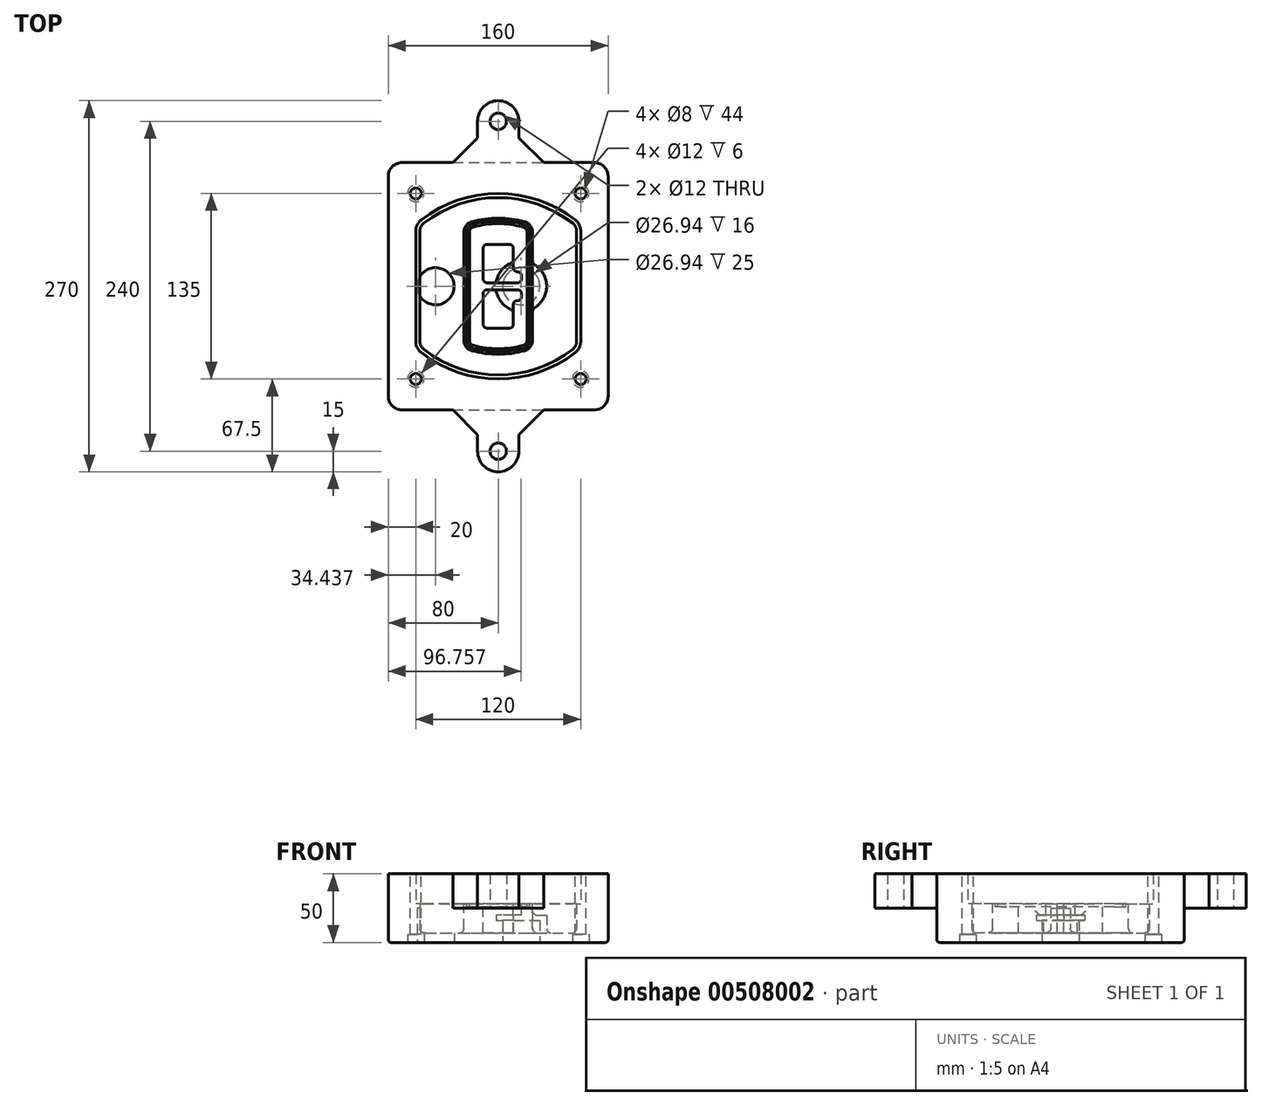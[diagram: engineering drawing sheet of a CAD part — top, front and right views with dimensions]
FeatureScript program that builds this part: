
annotation { "Feature Type Name" : "Feature", "Feature Type Description" : "" }
export const myFeature = defineFeature(function(context is Context, id is Id, definition is map)
    precondition{}
    {
        {
            var Q0;
            Q0=qCreatedBy(makeId("Top.planeOp"),FACE);
            var sketch = newSketch(context, id + "F0", { "sketchPlane" : qUnion([Q0])});
            skPoint(sketch, "E0.rect.middle", {"position": v(0, 0) * mm});
            skLineSegment(sketch, "E1.bottom", {"start": v(-70, -90) * mm, "end": v(70, -90) * mm});
            skLineSegment(sketch, "E1.top", {"start": v(-70, 90) * mm, "end": v(70, 90) * mm});
            skLineSegment(sketch, "E1.left", {"start": v(-80, -80) * mm, "end": v(-80, 80) * mm});
            skLineSegment(sketch, "E1.right", {"start": v(80, -80) * mm, "end": v(80, 80) * mm});
            skLineSegment(sketch, "E2", {"start": v(-80, 90) * mm, "end": v(80, -90) * mm, "construction": true});
            skLineSegment(sketch, "E3", {"start": v(80, 90) * mm, "end": v(-80, -90) * mm, "construction": true});
            skCircle(sketch, "E4", {"center": v(-60, 67.5) * mm, "radius": 4 * mm});
            skCircle(sketch, "E5", {"center": v(60, 67.5) * mm, "radius": 4 * mm});
            skCircle(sketch, "E6", {"center": v(60, -67.5) * mm, "radius": 4 * mm});
            skCircle(sketch, "E7", {"center": v(-60, -67.5) * mm, "radius": 4 * mm});
            skLineSegment(sketch, "E8", {"start": v(-60, 67.5) * mm, "end": v(60, 67.5) * mm, "construction": true});
            skLineSegment(sketch, "E9", {"start": v(60, 67.5) * mm, "end": v(60, -67.5) * mm, "construction": true});
            skLineSegment(sketch, "E10", {"start": v(60, -67.5) * mm, "end": v(-60, -67.5) * mm, "construction": true});
            skLineSegment(sketch, "E11", {"start": v(-60, -67.5) * mm, "end": v(-60, 67.5) * mm, "construction": true});
            skLineSegment(sketch, "E12", {"start": v(-60, 40.3) * mm, "end": v(-60, -40.3) * mm});
            skLineSegment(sketch, "E13", {"start": v(60, 40.3) * mm, "end": v(60, -40.3) * mm});
            skArc(sketch, "E14", {"start": v(56.15, 48.18) * mm, "mid": v(0, 67.5) * mm, "end": v(-56.15, 48.18) * mm});
            skArc(sketch, "E15", {"start": v(-56.15, -48.18) * mm, "mid": v(0, -67.5) * mm, "end": v(56.15, -48.18) * mm});
            skLineSegment(sketch, "E16", {"start": v(-60, 0) * mm, "end": v(60, 0) * mm, "construction": true});
            skPoint(sketch, "E17.visualSharp", {"position": v(-60, -45) * mm});
            skArc(sketch, "E17.filletArc", {"start": v(-60, -40.3) * mm, "mid": v(-58.99, -44.68) * mm, "end": v(-56.15, -48.18) * mm});
            skPoint(sketch, "E18.visualSharp", {"position": v(-60, 45) * mm});
            skArc(sketch, "E18.filletArc", {"start": v(-56.15, 48.18) * mm, "mid": v(-58.99, 44.68) * mm, "end": v(-60, 40.3) * mm});
            skPoint(sketch, "E19.visualSharp", {"position": v(60, 45) * mm});
            skArc(sketch, "E19.filletArc", {"start": v(60, 40.3) * mm, "mid": v(58.99, 44.68) * mm, "end": v(56.15, 48.18) * mm});
            skPoint(sketch, "E20.visualSharp", {"position": v(60, -45) * mm});
            skArc(sketch, "E20.filletArc", {"start": v(56.15, -48.18) * mm, "mid": v(58.99, -44.68) * mm, "end": v(60, -40.3) * mm});
            skPoint(sketch, "E21.visualSharp", {"position": v(-80, 90) * mm});
            skArc(sketch, "E21.filletArc", {"start": v(-70, 90) * mm, "mid": v(-77.07, 87.07) * mm, "end": v(-80, 80) * mm});
            skPoint(sketch, "E22.visualSharp", {"position": v(80, 90) * mm});
            skArc(sketch, "E22.filletArc", {"start": v(80, 80) * mm, "mid": v(77.07, 87.07) * mm, "end": v(70, 90) * mm});
            skPoint(sketch, "E23.visualSharp", {"position": v(80, -90) * mm});
            skArc(sketch, "E23.filletArc", {"start": v(70, -90) * mm, "mid": v(77.07, -87.07) * mm, "end": v(80, -80) * mm});
            skPoint(sketch, "E24.visualSharp", {"position": v(-80, -90) * mm});
            skArc(sketch, "E24.filletArc", {"start": v(-80, -80) * mm, "mid": v(-77.07, -87.07) * mm, "end": v(-70, -90) * mm});
            skArc(sketch, "E25.0", {"start": v(57, 40.3) * mm, "mid": v(56.3, 43.36) * mm, "end": v(54.3, 45.81) * mm});
            skLineSegment(sketch, "E25.1", {"start": v(57, 40.3) * mm, "end": v(57, -40.3) * mm});
            skArc(sketch, "E25.2", {"start": v(54.3, -45.81) * mm, "mid": v(56.3, -43.36) * mm, "end": v(57, -40.3) * mm});
            skArc(sketch, "E25.3", {"start": v(-54.3, -45.81) * mm, "mid": v(0, -64.5) * mm, "end": v(54.3, -45.81) * mm});
            skArc(sketch, "E25.4", {"start": v(-57, -40.3) * mm, "mid": v(-56.3, -43.36) * mm, "end": v(-54.3, -45.81) * mm});
            skArc(sketch, "E25.5", {"start": v(54.3, 45.81) * mm, "mid": v(0, 64.5) * mm, "end": v(-54.3, 45.81) * mm});
            skLineSegment(sketch, "E25.6", {"start": v(-57, 40.3) * mm, "end": v(-57, -40.3) * mm});
            skArc(sketch, "E25.7", {"start": v(-54.3, 45.81) * mm, "mid": v(-56.3, 43.36) * mm, "end": v(-57, 40.3) * mm});
            skArc(sketch, "E26.0", {"start": v(-58.62, 51.33) * mm, "mid": v(-62.58, 46.43) * mm, "end": v(-64, 40.3) * mm});
            skArc(sketch, "E26.1", {"start": v(58.62, 51.33) * mm, "mid": v(0, 71.5) * mm, "end": v(-58.62, 51.33) * mm});
            skArc(sketch, "E26.2", {"start": v(64, 40.3) * mm, "mid": v(62.58, 46.43) * mm, "end": v(58.62, 51.33) * mm});
            skLineSegment(sketch, "E26.3", {"start": v(64, 40.3) * mm, "end": v(64, -40.3) * mm});
            skArc(sketch, "E26.4", {"start": v(58.62, -51.33) * mm, "mid": v(62.58, -46.43) * mm, "end": v(64, -40.3) * mm});
            skLineSegment(sketch, "E26.5", {"start": v(-64, 40.3) * mm, "end": v(-64, -40.3) * mm});
            skArc(sketch, "E26.6", {"start": v(-58.62, -51.33) * mm, "mid": v(0, -71.5) * mm, "end": v(58.62, -51.33) * mm});
            skArc(sketch, "E26.7", {"start": v(-64, -40.3) * mm, "mid": v(-62.58, -46.43) * mm, "end": v(-58.62, -51.33) * mm});
            skSolve(sketch);
        }
        {
            var Q0;
            Q0=makeQuery(id+"F0.imprint","IMPRINT",FACE,{"disambiguationData":[TD([[makeQuery(id+"F0.imprint","IMPRINT",EDGE,{"derivedFrom":sQuery(id+"F0.wireOp",EDGE,"E1.bottom")}),1.0]])]});
            var Q1;
            Q1=makeQuery(id+"F0.imprint","IMPRINT",FACE,{"disambiguationData":[TD([[makeQuery(id+"F0.imprint","IMPRINT",EDGE,{"derivedFrom":sQuery(id+"F0.wireOp",EDGE,"E12")}),1.0]])]});
            var Q2;
            Q2=makeQuery(id+"F0.imprint","IMPRINT",FACE,{"disambiguationData":[TD([[makeQuery(id+"F0.imprint","IMPRINT",EDGE,{"derivedFrom":sQuery(id+"F0.wireOp",EDGE,"E25.0")}),1.0]])]});
            var Q3;
            Q3=makeQuery(id+"F0.imprint","IMPRINT",FACE,{"disambiguationData":[TD([[makeQuery(id+"F0.imprint","IMPRINT",EDGE,{"derivedFrom":sQuery(id+"F0.wireOp",EDGE,"E12")}),-1.0]])]});
            extrude(context, id + "F1", {"entities" : qUnion([Q0, Q1, Q2, Q3]), "oppositeDirection" : true, "depth" : 25 * mm});
        }
        {
            var Q0;
            Q0=makeQuery(id+"F0.imprint","IMPRINT",FACE,{"disambiguationData":[TD([[makeQuery(id+"F0.imprint","IMPRINT",EDGE,{"derivedFrom":sQuery(id+"F0.wireOp",EDGE,"E12")}),1.0]])]});
            extrude(context, id + "F2", {"entities" : qUnion([Q0]), "operationType" : NewBodyOperationType.ADD, "depth" : 3 * mm});
        }
        {
            var Q0;
            Q0=makeQuery(id+"F0.imprint","IMPRINT",FACE,{"disambiguationData":[TD([[makeQuery(id+"F0.imprint","IMPRINT",EDGE,{"derivedFrom":sQuery(id+"F0.wireOp",EDGE,"E25.0")}),1.0]])]});
            extrude(context, id + "F3", {"entities" : qUnion([Q0]), "operationType" : NewBodyOperationType.REMOVE, "oppositeDirection" : true, "depth" : 18 * mm});
        }
        {
            var Q0;
            Q0=makeQuery(id+"F2.opExtrude","CAP_FACE",FACE,{"disambiguationData":[OSD([sQuery(id+"F0.wireOp",EDGE,"E12"),sQuery(id+"F0.wireOp",EDGE,"E13"),sQuery(id+"F0.wireOp",EDGE,"E14"),sQuery(id+"F0.wireOp",EDGE,"E15"),sQuery(id+"F0.wireOp",EDGE,"E17.filletArc"),sQuery(id+"F0.wireOp",EDGE,"E18.filletArc"),sQuery(id+"F0.wireOp",EDGE,"E19.filletArc"),sQuery(id+"F0.wireOp",EDGE,"E20.filletArc"),sQuery(id+"F0.wireOp",EDGE,"E25.0"),sQuery(id+"F0.wireOp",EDGE,"E25.1"),sQuery(id+"F0.wireOp",EDGE,"E25.2"),sQuery(id+"F0.wireOp",EDGE,"E25.3"),sQuery(id+"F0.wireOp",EDGE,"E25.4"),sQuery(id+"F0.wireOp",EDGE,"E25.5"),sQuery(id+"F0.wireOp",EDGE,"E25.6"),sQuery(id+"F0.wireOp",EDGE,"E25.7")])],"isStart":false});
            var sketch = newSketch(context, id + "F4", { "sketchPlane" : qUnion([Q0])});
            skArc(sketch, "E27.0", {"start": v(-19.08, -46.97) * mm, "mid": v(0, -49.5) * mm, "end": v(19.08, -46.97) * mm});
            skArc(sketch, "E28.0", {"start": v(19.08, 46.97) * mm, "mid": v(0, 49.5) * mm, "end": v(-19.08, 46.97) * mm});
            skLineSegment(sketch, "E29", {"start": v(-25, 39.25) * mm, "end": v(-25, -39.25) * mm});
            skLineSegment(sketch, "E30", {"start": v(25, 39.25) * mm, "end": v(25, -39.25) * mm});
            skLineSegment(sketch, "E31", {"start": v(-25, 45.1) * mm, "end": v(25, 45.1) * mm, "construction": true});
            skLineSegment(sketch, "E32", {"start": v(-25, -45.1) * mm, "end": v(25, -45.1) * mm, "construction": true});
            skPoint(sketch, "E33.visualSharp", {"position": v(-25, 45.1) * mm});
            skArc(sketch, "E33.filletArc", {"start": v(-19.08, 46.97) * mm, "mid": v(-23.35, 44.11) * mm, "end": v(-25, 39.25) * mm});
            skPoint(sketch, "E34.visualSharp", {"position": v(25, 45.1) * mm});
            skArc(sketch, "E34.filletArc", {"start": v(25, 39.25) * mm, "mid": v(23.35, 44.11) * mm, "end": v(19.08, 46.97) * mm});
            skPoint(sketch, "E35.visualSharp", {"position": v(25, -45.1) * mm});
            skArc(sketch, "E35.filletArc", {"start": v(19.08, -46.97) * mm, "mid": v(23.35, -44.11) * mm, "end": v(25, -39.25) * mm});
            skPoint(sketch, "E36.visualSharp", {"position": v(-25, -45.1) * mm});
            skArc(sketch, "E36.filletArc", {"start": v(-25, -39.25) * mm, "mid": v(-23.35, -44.11) * mm, "end": v(-19.08, -46.97) * mm});
            skArc(sketch, "E37.0", {"start": v(54.3, 45.81) * mm, "mid": v(0, 64.5) * mm, "end": v(-54.3, 45.81) * mm});
            skArc(sketch, "E37.1", {"start": v(-54.3, 45.81) * mm, "mid": v(-56.3, 43.36) * mm, "end": v(-57, 40.3) * mm});
            skLineSegment(sketch, "E37.2", {"start": v(-57, 40.3) * mm, "end": v(-57, -40.3) * mm});
            skArc(sketch, "E37.3", {"start": v(-57, -40.3) * mm, "mid": v(-56.3, -43.36) * mm, "end": v(-54.3, -45.81) * mm});
            skArc(sketch, "E37.4", {"start": v(-54.3, -45.81) * mm, "mid": v(0, -64.5) * mm, "end": v(54.3, -45.81) * mm});
            skArc(sketch, "E37.5", {"start": v(54.3, -45.81) * mm, "mid": v(56.3, -43.36) * mm, "end": v(57, -40.3) * mm});
            skLineSegment(sketch, "E37.6", {"start": v(57, 40.3) * mm, "end": v(57, -40.3) * mm});
            skArc(sketch, "E37.7", {"start": v(57, 40.3) * mm, "mid": v(56.3, 43.36) * mm, "end": v(54.3, 45.81) * mm});
            skLineSegment(sketch, "E38.0", {"start": v(23, 39.25) * mm, "end": v(23, -39.25) * mm});
            skArc(sketch, "E38.1", {"start": v(18.56, -45.04) * mm, "mid": v(21.76, -42.9) * mm, "end": v(23, -39.25) * mm});
            skArc(sketch, "E38.2", {"start": v(-18.56, -45.04) * mm, "mid": v(0, -47.5) * mm, "end": v(18.56, -45.04) * mm});
            skArc(sketch, "E38.3", {"start": v(-23, -39.25) * mm, "mid": v(-21.76, -42.9) * mm, "end": v(-18.56, -45.04) * mm});
            skLineSegment(sketch, "E38.4", {"start": v(-23, 39.25) * mm, "end": v(-23, -39.25) * mm});
            skArc(sketch, "E38.5", {"start": v(23, 39.25) * mm, "mid": v(21.76, 42.9) * mm, "end": v(18.56, 45.04) * mm});
            skArc(sketch, "E38.6", {"start": v(-18.56, 45.04) * mm, "mid": v(-21.76, 42.9) * mm, "end": v(-23, 39.25) * mm});
            skArc(sketch, "E38.7", {"start": v(18.56, 45.04) * mm, "mid": v(0, 47.5) * mm, "end": v(-18.56, 45.04) * mm});
            skArc(sketch, "E39.0", {"start": v(21, 39.25) * mm, "mid": v(20.18, 41.68) * mm, "end": v(18.04, 43.1) * mm});
            skLineSegment(sketch, "E39.1", {"start": v(21, 39.25) * mm, "end": v(21, -39.25) * mm});
            skArc(sketch, "E39.2", {"start": v(18.04, -43.1) * mm, "mid": v(20.18, -41.68) * mm, "end": v(21, -39.25) * mm});
            skArc(sketch, "E39.3", {"start": v(-18.04, -43.1) * mm, "mid": v(0, -45.5) * mm, "end": v(18.04, -43.1) * mm});
            skArc(sketch, "E39.4", {"start": v(-21, -39.25) * mm, "mid": v(-20.18, -41.68) * mm, "end": v(-18.04, -43.1) * mm});
            skArc(sketch, "E39.5", {"start": v(18.04, 43.1) * mm, "mid": v(0, 45.5) * mm, "end": v(-18.04, 43.1) * mm});
            skLineSegment(sketch, "E39.6", {"start": v(-21, 39.25) * mm, "end": v(-21, -39.25) * mm});
            skArc(sketch, "E39.7", {"start": v(-18.04, 43.1) * mm, "mid": v(-20.18, 41.68) * mm, "end": v(-21, 39.25) * mm});
            skLineSegment(sketch, "E40", {"start": v(-25, 0) * mm, "end": v(25, 0) * mm, "construction": true});
            skLineSegment(sketch, "E41", {"start": v(-11, 5.5) * mm, "end": v(-11, 27.5) * mm});
            skLineSegment(sketch, "E42", {"start": v(-8, 30.5) * mm, "end": v(8, 30.5) * mm});
            skLineSegment(sketch, "E43", {"start": v(11, 27.5) * mm, "end": v(11, 13.5) * mm});
            skLineSegment(sketch, "E44", {"start": v(14, 10.5) * mm, "end": v(14, 10.5) * mm});
            skLineSegment(sketch, "E45", {"start": v(17, 7.5) * mm, "end": v(17, 5.5) * mm});
            skLineSegment(sketch, "E46", {"start": v(14, 2.5) * mm, "end": v(-8, 2.5) * mm});
            skPoint(sketch, "E47.visualSharp", {"position": v(-11, 30.5) * mm});
            skArc(sketch, "E47.filletArc", {"start": v(-8, 30.5) * mm, "mid": v(-10.12, 29.62) * mm, "end": v(-11, 27.5) * mm});
            skPoint(sketch, "E48.visualSharp", {"position": v(11, 30.5) * mm});
            skArc(sketch, "E48.filletArc", {"start": v(11, 27.5) * mm, "mid": v(10.12, 29.62) * mm, "end": v(8, 30.5) * mm});
            skPoint(sketch, "E49.visualSharp", {"position": v(11, 10.5) * mm});
            skArc(sketch, "E49.filletArc", {"start": v(11, 13.5) * mm, "mid": v(11.88, 11.38) * mm, "end": v(14, 10.5) * mm});
            skPoint(sketch, "E50.visualSharp", {"position": v(17, 10.5) * mm});
            skArc(sketch, "E50.filletArc", {"start": v(17, 7.5) * mm, "mid": v(16.12, 9.62) * mm, "end": v(14, 10.5) * mm});
            skPoint(sketch, "E51.visualSharp", {"position": v(17, 2.5) * mm});
            skArc(sketch, "E51.filletArc", {"start": v(14, 2.5) * mm, "mid": v(16.12, 3.38) * mm, "end": v(17, 5.5) * mm});
            skPoint(sketch, "E52.visualSharp", {"position": v(-11, 2.5) * mm});
            skArc(sketch, "E52.filletArc", {"start": v(-11, 5.5) * mm, "mid": v(-10.12, 3.38) * mm, "end": v(-8, 2.5) * mm});
            skLineSegment(sketch, "E53.0.MirrorCS", {"start": v(14, -2.5) * mm, "end": v(-8, -2.5) * mm});
            skArc(sketch, "E54.0.MirrorCS", {"start": v(-11, -5.5) * mm, "mid": v(-10.12, -3.38) * mm, "end": v(-8, -2.5) * mm});
            skLineSegment(sketch, "E55.0.MirrorCS", {"start": v(-11, -5.5) * mm, "end": v(-11, -27.5) * mm});
            skArc(sketch, "E56.0.MirrorCS", {"start": v(-8, -30.5) * mm, "mid": v(-10.12, -29.62) * mm, "end": v(-11, -27.5) * mm});
            skLineSegment(sketch, "E57.0.MirrorCS", {"start": v(-8, -30.5) * mm, "end": v(8, -30.5) * mm});
            skArc(sketch, "E58.0.MirrorCS", {"start": v(11, -27.5) * mm, "mid": v(10.12, -29.62) * mm, "end": v(8, -30.5) * mm});
            skLineSegment(sketch, "E59.0.MirrorCS", {"start": v(11, -27.5) * mm, "end": v(11, -13.5) * mm});
            skArc(sketch, "E60.0.MirrorCS", {"start": v(11, -13.5) * mm, "mid": v(11.88, -11.38) * mm, "end": v(14, -10.5) * mm});
            skArc(sketch, "E61.0.MirrorCS", {"start": v(17, -7.5) * mm, "mid": v(16.12, -9.62) * mm, "end": v(14, -10.5) * mm});
            skLineSegment(sketch, "E62.0.MirrorCS", {"start": v(17, -7.5) * mm, "end": v(17, -5.5) * mm});
            skArc(sketch, "E63.0.MirrorCS", {"start": v(14, -2.5) * mm, "mid": v(16.12, -3.38) * mm, "end": v(17, -5.5) * mm});
            skSolve(sketch);
        }
        {
            var Q0;
            Q0=makeQuery(id+"F4.imprint","IMPRINT",FACE,{"disambiguationData":[TD([[makeQuery(id+"F4.imprint","IMPRINT",EDGE,{"derivedFrom":sQuery(id+"F4.wireOp",EDGE,"E27.0")}),1.0]])]});
            var Q1;
            Q1=makeQuery(id+"F4.imprint","IMPRINT",FACE,{"disambiguationData":[TD([[makeQuery(id+"F4.imprint","IMPRINT",EDGE,{"derivedFrom":sQuery(id+"F4.wireOp",EDGE,"E38.0")}),-1.0]])]});
            var Q2;
            Q2=makeQuery(id+"F4.imprint","IMPRINT",FACE,{"disambiguationData":[TD([[makeQuery(id+"F4.imprint","IMPRINT",EDGE,{"derivedFrom":sQuery(id+"F4.wireOp",EDGE,"E39.0")}),1.0]])]});
            extrude(context, id + "F5", {"entities" : qUnion([Q0, Q1, Q2]), "operationType" : NewBodyOperationType.ADD, "endBound" : BoundingType.UP_TO_NEXT, "oppositeDirection" : true, "depth" : 25 * mm});
        }
        {
            var Q0;
            Q0=makeQuery(id+"F4.imprint","IMPRINT",FACE,{"disambiguationData":[TD([[makeQuery(id+"F4.imprint","IMPRINT",EDGE,{"derivedFrom":sQuery(id+"F4.wireOp",EDGE,"E38.0")}),-1.0]])]});
            extrude(context, id + "F6", {"entities" : qUnion([Q0]), "operationType" : NewBodyOperationType.REMOVE, "oppositeDirection" : true, "depth" : 2 * mm});
        }
        {
            var Q0;
            Q0=makeQuery(id+"F1.opExtrude","CAP_FACE",FACE,{"disambiguationData":[OSD([sQuery(id+"F0.wireOp",EDGE,"E1.bottom"),sQuery(id+"F0.wireOp",EDGE,"E1.top"),sQuery(id+"F0.wireOp",EDGE,"E1.left"),sQuery(id+"F0.wireOp",EDGE,"E1.right"),sQuery(id+"F0.wireOp",EDGE,"E4"),sQuery(id+"F0.wireOp",EDGE,"E5"),sQuery(id+"F0.wireOp",EDGE,"E6"),sQuery(id+"F0.wireOp",EDGE,"E7"),sQuery(id+"F0.wireOp",EDGE,"E21.filletArc"),sQuery(id+"F0.wireOp",EDGE,"E22.filletArc"),sQuery(id+"F0.wireOp",EDGE,"E23.filletArc"),sQuery(id+"F0.wireOp",EDGE,"E24.filletArc")])],"isStart":false});
            var sketch = newSketch(context, id + "F7", { "sketchPlane" : qUnion([Q0])});
            skCircle(sketch, "E64", {"center": v(16.76, 0) * mm, "radius": 13.47 * mm});
            skCircle(sketch, "E65", {"center": v(-45.56, 0) * mm, "radius": 13.47 * mm});
            skLineSegment(sketch, "E66", {"start": v(80, 0) * mm, "end": v(-80, 0) * mm});
            skCircle(sketch, "E67", {"center": v(16.76, 0) * mm, "radius": 18.47 * mm});
            skCircle(sketch, "E68", {"center": v(60, -67.5) * mm, "radius": 6 * mm});
            skCircle(sketch, "E69", {"center": v(-60, -67.5) * mm, "radius": 6 * mm});
            skCircle(sketch, "E70", {"center": v(-60, 67.5) * mm, "radius": 6 * mm});
            skCircle(sketch, "E71", {"center": v(60, 67.5) * mm, "radius": 6 * mm});
            skSolve(sketch);
        }
        {
            var Q0;
            {var subQ1=sQuery(id+"F7.wireOp",EDGE,"E66");var subQ4=sQuery(id+"F7.wireOp",EDGE,"E64");var subQ6=makeQuery(id+"F7.imprint","INTERSECT",VERTEX,{"disambiguationData":[OD(0.0)],"derivedFrom":[subQ4,subQ1]});Q0=makeQuery(id+"F7.imprint","IMPRINT",FACE,{"disambiguationData":[TD([[makeQuery(id+"F7.imprint","IMPRINT",EDGE,{"disambiguationData":[TD([[subQ6,-1.0]])],"derivedFrom":subQ4}),-1.0]])]});}
            var Q1;
            {var subQ0=sQuery(id+"F7.wireOp",EDGE,"E66");var subQ1=sQuery(id+"F7.wireOp",EDGE,"E64");var subQ3=makeQuery(id+"F7.imprint","INTERSECT",VERTEX,{"disambiguationData":[OD(0.0)],"derivedFrom":[subQ1,subQ0]});Q1=makeQuery(id+"F7.imprint","IMPRINT",FACE,{"disambiguationData":[TD([[makeQuery(id+"F7.imprint","IMPRINT",EDGE,{"disambiguationData":[TD([[subQ3,-1.0]])],"derivedFrom":subQ1}),1.0]])]});}
            var Q2;
            {var subQ0=sQuery(id+"F7.wireOp",EDGE,"E66");var subQ1=sQuery(id+"F7.wireOp",EDGE,"E64");var subQ3=makeQuery(id+"F7.imprint","INTERSECT",VERTEX,{"disambiguationData":[OD(0.0)],"derivedFrom":[subQ1,subQ0]});Q2=makeQuery(id+"F7.imprint","IMPRINT",FACE,{"disambiguationData":[TD([[makeQuery(id+"F7.imprint","IMPRINT",EDGE,{"disambiguationData":[TD([[subQ3,1.0]])],"derivedFrom":subQ1}),1.0]])]});}
            var Q3;
            {var subQ1=sQuery(id+"F7.wireOp",EDGE,"E66");var subQ4=sQuery(id+"F7.wireOp",EDGE,"E64");var subQ6=makeQuery(id+"F7.imprint","INTERSECT",VERTEX,{"disambiguationData":[OD(0.0)],"derivedFrom":[subQ4,subQ1]});Q3=makeQuery(id+"F7.imprint","IMPRINT",FACE,{"disambiguationData":[TD([[makeQuery(id+"F7.imprint","IMPRINT",EDGE,{"disambiguationData":[TD([[subQ6,1.0]])],"derivedFrom":subQ4}),-1.0]])]});}
            extrude(context, id + "F8", {"entities" : qUnion([Q0, Q1, Q2, Q3]), "operationType" : NewBodyOperationType.ADD, "oppositeDirection" : true, "depth" : 20 * mm});
        }
        {
            var Q0;
            {var subQ0=sQuery(id+"F7.wireOp",EDGE,"E66");var subQ1=sQuery(id+"F7.wireOp",EDGE,"E64");var subQ3=makeQuery(id+"F7.imprint","INTERSECT",VERTEX,{"disambiguationData":[OD(0.0)],"derivedFrom":[subQ1,subQ0]});Q0=makeQuery(id+"F7.imprint","IMPRINT",FACE,{"disambiguationData":[TD([[makeQuery(id+"F7.imprint","IMPRINT",EDGE,{"disambiguationData":[TD([[subQ3,-1.0]])],"derivedFrom":subQ1}),1.0]])]});}
            var Q1;
            {var subQ0=sQuery(id+"F7.wireOp",EDGE,"E66");var subQ1=sQuery(id+"F7.wireOp",EDGE,"E64");var subQ3=makeQuery(id+"F7.imprint","INTERSECT",VERTEX,{"disambiguationData":[OD(0.0)],"derivedFrom":[subQ1,subQ0]});Q1=makeQuery(id+"F7.imprint","IMPRINT",FACE,{"disambiguationData":[TD([[makeQuery(id+"F7.imprint","IMPRINT",EDGE,{"disambiguationData":[TD([[subQ3,1.0]])],"derivedFrom":subQ1}),1.0]])]});}
            extrude(context, id + "F9", {"entities" : qUnion([Q0, Q1]), "operationType" : NewBodyOperationType.REMOVE, "oppositeDirection" : true, "depth" : 16 * mm});
        }
        {
            var Q0;
            {var subQ0=sQuery(id+"F7.wireOp",EDGE,"E66");var subQ1=sQuery(id+"F7.wireOp",EDGE,"E65");var subQ3=makeQuery(id+"F7.imprint","INTERSECT",VERTEX,{"disambiguationData":[OD(0.0)],"derivedFrom":[subQ1,subQ0]});Q0=makeQuery(id+"F7.imprint","IMPRINT",FACE,{"disambiguationData":[TD([[makeQuery(id+"F7.imprint","IMPRINT",EDGE,{"disambiguationData":[TD([[subQ3,-1.0]])],"derivedFrom":subQ1}),1.0]])]});}
            var Q1;
            {var subQ0=sQuery(id+"F7.wireOp",EDGE,"E66");var subQ1=sQuery(id+"F7.wireOp",EDGE,"E65");var subQ3=makeQuery(id+"F7.imprint","INTERSECT",VERTEX,{"disambiguationData":[OD(0.0)],"derivedFrom":[subQ1,subQ0]});Q1=makeQuery(id+"F7.imprint","IMPRINT",FACE,{"disambiguationData":[TD([[makeQuery(id+"F7.imprint","IMPRINT",EDGE,{"disambiguationData":[TD([[subQ3,1.0]])],"derivedFrom":subQ1}),1.0]])]});}
            extrude(context, id + "F10", {"entities" : qUnion([Q0, Q1]), "operationType" : NewBodyOperationType.REMOVE, "oppositeDirection" : true, "depth" : 25 * mm});
        }
        {
            var Q0;
            Q0=makeQuery(id+"F7.imprint","IMPRINT",FACE,{"disambiguationData":[TD([[makeQuery(id+"F7.imprint","IMPRINT",EDGE,{"derivedFrom":sQuery(id+"F7.wireOp",EDGE,"E68")}),1.0]])]});
            var Q1;
            Q1=makeQuery(id+"F7.imprint","IMPRINT",FACE,{"disambiguationData":[TD([[makeQuery(id+"F7.imprint","IMPRINT",EDGE,{"derivedFrom":makeQuery(id+"F1.opExtrude","CAP_EDGE",EDGE,{"disambiguationData":[OSD([sQuery(id+"F0.wireOp",EDGE,"E5")])],"isStart":false})}),-1.0]])]});
            var Q2;
            Q2=makeQuery(id+"F7.imprint","IMPRINT",FACE,{"disambiguationData":[TD([[makeQuery(id+"F7.imprint","IMPRINT",EDGE,{"derivedFrom":sQuery(id+"F7.wireOp",EDGE,"E69")}),1.0]])]});
            var Q3;
            Q3=makeQuery(id+"F7.imprint","IMPRINT",FACE,{"disambiguationData":[TD([[makeQuery(id+"F7.imprint","IMPRINT",EDGE,{"derivedFrom":makeQuery(id+"F1.opExtrude","CAP_EDGE",EDGE,{"disambiguationData":[OSD([sQuery(id+"F0.wireOp",EDGE,"E4")])],"isStart":false})}),-1.0]])]});
            var Q4;
            Q4=makeQuery(id+"F7.imprint","IMPRINT",FACE,{"disambiguationData":[TD([[makeQuery(id+"F7.imprint","IMPRINT",EDGE,{"derivedFrom":sQuery(id+"F7.wireOp",EDGE,"E70")}),1.0]])]});
            var Q5;
            Q5=makeQuery(id+"F7.imprint","IMPRINT",FACE,{"disambiguationData":[TD([[makeQuery(id+"F7.imprint","IMPRINT",EDGE,{"derivedFrom":makeQuery(id+"F1.opExtrude","CAP_EDGE",EDGE,{"disambiguationData":[OSD([sQuery(id+"F0.wireOp",EDGE,"E7")])],"isStart":false})}),-1.0]])]});
            var Q6;
            Q6=makeQuery(id+"F7.imprint","IMPRINT",FACE,{"disambiguationData":[TD([[makeQuery(id+"F7.imprint","IMPRINT",EDGE,{"derivedFrom":sQuery(id+"F7.wireOp",EDGE,"E71")}),1.0]])]});
            var Q7;
            Q7=makeQuery(id+"F7.imprint","IMPRINT",FACE,{"disambiguationData":[TD([[makeQuery(id+"F7.imprint","IMPRINT",EDGE,{"derivedFrom":makeQuery(id+"F1.opExtrude","CAP_EDGE",EDGE,{"disambiguationData":[OSD([sQuery(id+"F0.wireOp",EDGE,"E6")])],"isStart":false})}),-1.0]])]});
            extrude(context, id + "F11", {"entities" : qUnion([Q0, Q1, Q2, Q3, Q4, Q5, Q6, Q7]), "operationType" : NewBodyOperationType.REMOVE, "oppositeDirection" : true, "depth" : 6 * mm});
        }
        {
            var Q0;
            Q0=makeQuery(id+"F9.boolean.opBoolean","COPY",FACE,{"derivedFrom":makeQuery(id+"F9.opExtrude","CAP_FACE",FACE,{"disambiguationData":[OSD([sQuery(id+"F7.wireOp",EDGE,"E64")])],"isStart":false})});
            var sketch = newSketch(context, id + "F12", { "sketchPlane" : qUnion([Q0])});
            skArc(sketch, "E72.0", {"start": v(11, 17.55) * mm, "mid": v(2.57, 11.82) * mm, "end": v(-1.54, 2.5) * mm});
            skArc(sketch, "E72.1", {"start": v(-1.54, -2.5) * mm, "mid": v(2.57, -11.82) * mm, "end": v(11, -17.55) * mm});
            skLineSegment(sketch, "E73", {"start": v(-1.54, -2.5) * mm, "end": v(14, -2.5) * mm});
            skLineSegment(sketch, "E74.0", {"start": v(14, 2.5) * mm, "end": v(-1.54, 2.5) * mm});
            skArc(sketch, "E74.1", {"start": v(14, 2.5) * mm, "mid": v(16.12, 3.38) * mm, "end": v(17, 5.5) * mm});
            skLineSegment(sketch, "E74.2", {"start": v(17, 7.5) * mm, "end": v(17, 5.5) * mm});
            skArc(sketch, "E74.3", {"start": v(17, 7.5) * mm, "mid": v(16.12, 9.62) * mm, "end": v(14, 10.5) * mm});
            skArc(sketch, "E74.4", {"start": v(11, 13.5) * mm, "mid": v(11.88, 11.38) * mm, "end": v(14, 10.5) * mm});
            skLineSegment(sketch, "E74.5", {"start": v(11, 17.55) * mm, "end": v(11, 13.5) * mm});
            skLineSegment(sketch, "E74.7", {"start": v(14, -2.5) * mm, "end": v(-1.54, -2.5) * mm});
            skArc(sketch, "E74.8", {"start": v(14, -2.5) * mm, "mid": v(16.12, -3.38) * mm, "end": v(17, -5.5) * mm});
            skLineSegment(sketch, "E74.9", {"start": v(17, -7.5) * mm, "end": v(17, -5.5) * mm});
            skArc(sketch, "E74.10", {"start": v(17, -7.5) * mm, "mid": v(16.12, -9.62) * mm, "end": v(14, -10.5) * mm});
            skArc(sketch, "E74.11", {"start": v(11, -13.5) * mm, "mid": v(11.88, -11.38) * mm, "end": v(14, -10.5) * mm});
            skLineSegment(sketch, "E74.12", {"start": v(11, -17.55) * mm, "end": v(11, -13.5) * mm});
            skPoint(sketch, "E75.orphan", {"position": v(11, -27.5) * mm});
            skPoint(sketch, "E76.orphan", {"position": v(-8, -2.5) * mm});
            skPoint(sketch, "E77.orphan", {"position": v(-8, 2.5) * mm});
            skPoint(sketch, "E78.orphan", {"position": v(11, 27.5) * mm});
            skSolve(sketch);
        }
        {
            var Q0;
            {var subQ7=sQuery(id+"F12.wireOp",EDGE,"E72.0");var subQ14=sQuery(id+"F12.wireOp",EDGE,"E72.1");var subQ16=sQuery(id+"F12.wireOp",EDGE,"E74.1");var subQ18=sQuery(id+"F12.wireOp",EDGE,"E74.8");Q0=qUnion([makeQuery(id+"F12.imprint","IMPRINT",FACE,{"disambiguationData":[TD([[makeQuery(id+"F12.imprint","IMPRINT",EDGE,{"derivedFrom":subQ7}),1.0]])]}),makeQuery(id+"F12.imprint","IMPRINT",FACE,{"disambiguationData":[TD([[makeQuery(id+"F12.imprint","IMPRINT",EDGE,{"derivedFrom":subQ14}),1.0]])]}),makeQuery(id+"F12.imprint","IMPRINT",FACE,{"disambiguationData":[TD([[makeQuery(id+"F12.imprint","IMPRINT",EDGE,{"derivedFrom":subQ16}),1.0]])]}),makeQuery(id+"F12.imprint","IMPRINT",FACE,{"disambiguationData":[TD([[makeQuery(id+"F12.imprint","IMPRINT",EDGE,{"derivedFrom":subQ18}),-1.0]])]})]);}
            var Q1;
            Q1=makeQuery(id+"F5.boolean.opBoolean","SPLIT",FACE,{"disambiguationData":[TD([makeQuery(id+"F5.opExtrude","SWEPT_FACE",FACE,{"disambiguationData":[OSD([sQuery(id+"F4.wireOp",EDGE,"E41")])]})])],"derivedFrom":makeQuery(id+"F3.boolean.opBoolean","COPY",FACE,{"derivedFrom":makeQuery(id+"F3.opExtrude","CAP_FACE",FACE,{"disambiguationData":[OSD([sQuery(id+"F0.wireOp",EDGE,"E25.0"),sQuery(id+"F0.wireOp",EDGE,"E25.1"),sQuery(id+"F0.wireOp",EDGE,"E25.2"),sQuery(id+"F0.wireOp",EDGE,"E25.3"),sQuery(id+"F0.wireOp",EDGE,"E25.4"),sQuery(id+"F0.wireOp",EDGE,"E25.5"),sQuery(id+"F0.wireOp",EDGE,"E25.6"),sQuery(id+"F0.wireOp",EDGE,"E25.7")])],"isStart":false})})});
            extrude(context, id + "F13", {"entities" : qUnion([Q0]), "operationType" : NewBodyOperationType.REMOVE, "endBound" : BoundingType.UP_TO_SURFACE, "endBoundEntityFace" : qUnion([Q1]), "depth" : 25 * mm});
        }
        {
            var Q0;
            Q0=makeQuery(id+"F3.boolean.opBoolean","COPY",EDGE,{"derivedFrom":makeQuery(id+"F3.opExtrude","CAP_EDGE",EDGE,{"disambiguationData":[OSD([sQuery(id+"F0.wireOp",EDGE,"E25.6")])],"isStart":false})});
            var Q1;
            Q1=makeQuery(id+"F8.boolean.opBoolean","INTERSECT",EDGE,{"derivedFrom":[makeQuery(id+"F5.opExtrude","SWEPT_FACE",FACE,{"disambiguationData":[OSD([sQuery(id+"F4.wireOp",EDGE,"E30")])]}),makeQuery(id+"F8.opExtrude","CAP_FACE",FACE,{"disambiguationData":[OSD([sQuery(id+"F7.wireOp",EDGE,"E67")])],"isStart":false})]});
            var Q2;
            Q2=makeQuery(id+"F8.boolean.opBoolean","INTERSECT",EDGE,{"disambiguationData":[OD(1.0)],"derivedFrom":[makeQuery(id+"F5.opExtrude","SWEPT_FACE",FACE,{"disambiguationData":[OSD([sQuery(id+"F4.wireOp",EDGE,"E30")])]}),makeQuery(id+"F8.opExtrude","SWEPT_FACE",FACE,{"disambiguationData":[OSD([sQuery(id+"F7.wireOp",EDGE,"E67")])]})]});
            var Q3;
            {var subQ0=sQuery(id+"F4.wireOp",EDGE,"E30");Q3=makeQuery(id+"F8.boolean.opBoolean","SPLIT",EDGE,{"disambiguationData":[TD([makeQuery(id+"F5.opExtrude","SWEPT_FACE",FACE,{"disambiguationData":[OSD([sQuery(id+"F4.wireOp",EDGE,"E35.filletArc")])]})])],"derivedFrom":makeQuery(id+"F5.opExtrude","CAP_EDGE",EDGE,{"disambiguationData":[OSD([subQ0])],"isStart":false})});}
            var Q4;
            {var subQ0=sQuery(id+"F0.wireOp",EDGE,"E25.7");var subQ1=sQuery(id+"F0.wireOp",EDGE,"E25.1");var subQ2=sQuery(id+"F0.wireOp",EDGE,"E25.6");var subQ3=sQuery(id+"F0.wireOp",EDGE,"E25.5");var subQ4=sQuery(id+"F0.wireOp",EDGE,"E25.4");var subQ5=sQuery(id+"F0.wireOp",EDGE,"E25.0");var subQ6=sQuery(id+"F0.wireOp",EDGE,"E25.2");var subQ7=sQuery(id+"F0.wireOp",EDGE,"E25.3");Q4=makeQuery(id+"F8.boolean.opBoolean","INTERSECT",EDGE,{"derivedFrom":[makeQuery(id+"F5.boolean.opBoolean","SPLIT",FACE,{"disambiguationData":[TD([makeQuery(id+"F2.opExtrude","SWEPT_FACE",FACE,{"disambiguationData":[OSD([subQ5])]})])],"derivedFrom":makeQuery(id+"F3.boolean.opBoolean","COPY",FACE,{"derivedFrom":makeQuery(id+"F3.opExtrude","CAP_FACE",FACE,{"disambiguationData":[OSD([subQ5,subQ1,subQ6,subQ7,subQ4,subQ3,subQ2,subQ0])],"isStart":false})})}),makeQuery(id+"F8.opExtrude","SWEPT_FACE",FACE,{"disambiguationData":[OSD([sQuery(id+"F7.wireOp",EDGE,"E67")])]})]});}
            var Q5;
            Q5=makeQuery(id+"F8.boolean.opBoolean","INTERSECT",EDGE,{"disambiguationData":[OD(0.0)],"derivedFrom":[makeQuery(id+"F5.opExtrude","SWEPT_FACE",FACE,{"disambiguationData":[OSD([sQuery(id+"F4.wireOp",EDGE,"E30")])]}),makeQuery(id+"F8.opExtrude","SWEPT_FACE",FACE,{"disambiguationData":[OSD([sQuery(id+"F7.wireOp",EDGE,"E67")])]})]});
            fillet(context, id + "F14", {"entities" : qUnion([Q0, Q1, Q2, Q3, Q4, Q5]), "radius" : 3 * mm, "tangentPropagation" : true, "allowEdgeOverflow" : false});
        }
        {
            var Q0;
            Q0=makeQuery(id+"F1.opExtrude","CAP_EDGE",EDGE,{"disambiguationData":[OSD([sQuery(id+"F0.wireOp",EDGE,"E1.bottom")])],"isStart":false});
            fillet(context, id + "F15", {"entities" : qUnion([Q0]), "radius" : 2 * mm, "tangentPropagation" : true, "allowEdgeOverflow" : false});
        }
        {
            var Q0;
            {var subQ0=sQuery(id+"F0.wireOp",EDGE,"E21.filletArc");var subQ1=sQuery(id+"F0.wireOp",EDGE,"E7");var subQ2=sQuery(id+"F0.wireOp",EDGE,"E6");var subQ3=sQuery(id+"F0.wireOp",EDGE,"E5");var subQ4=sQuery(id+"F0.wireOp",EDGE,"E4");var subQ5=sQuery(id+"F0.wireOp",EDGE,"E22.filletArc");var subQ6=sQuery(id+"F0.wireOp",EDGE,"E1.bottom");var subQ7=sQuery(id+"F0.wireOp",EDGE,"E1.right");var subQ8=sQuery(id+"F0.wireOp",EDGE,"E1.top");var subQ9=sQuery(id+"F0.wireOp",EDGE,"E1.left");var subQ10=sQuery(id+"F0.wireOp",EDGE,"E23.filletArc");var subQ11=sQuery(id+"F0.wireOp",EDGE,"E24.filletArc");Q0=makeQuery(id+"F2.boolean.opBoolean","SPLIT",FACE,{"disambiguationData":[TD([makeQuery(id+"F1.opExtrude","SWEPT_FACE",FACE,{"disambiguationData":[OSD([subQ6])]})])],"derivedFrom":makeQuery(id+"F1.opExtrude","CAP_FACE",FACE,{"disambiguationData":[OSD([subQ6,subQ8,subQ9,subQ7,subQ4,subQ3,subQ2,subQ1,subQ0,subQ5,subQ10,subQ11])],"isStart":true})});}
            var sketch = newSketch(context, id + "F16", { "sketchPlane" : qUnion([Q0])});
            skLineSegment(sketch, "E79.0", {"start": v(-70, 90) * mm, "end": v(70, 90) * mm});
            skArc(sketch, "E79.1", {"start": v(-70, 90) * mm, "mid": v(-77.07, 87.07) * mm, "end": v(-80, 80) * mm});
            skLineSegment(sketch, "E79.2", {"start": v(-80, -80) * mm, "end": v(-80, 80) * mm});
            skArc(sketch, "E79.3", {"start": v(-80, -80) * mm, "mid": v(-77.07, -87.07) * mm, "end": v(-70, -90) * mm});
            skLineSegment(sketch, "E79.4", {"start": v(-70, -90) * mm, "end": v(70, -90) * mm});
            skArc(sketch, "E79.5", {"start": v(70, -90) * mm, "mid": v(77.07, -87.07) * mm, "end": v(80, -80) * mm});
            skLineSegment(sketch, "E79.6", {"start": v(80, -80) * mm, "end": v(80, 80) * mm});
            skArc(sketch, "E79.7", {"start": v(80, 80) * mm, "mid": v(77.07, 87.07) * mm, "end": v(70, 90) * mm});
            skArc(sketch, "E79.8", {"start": v(56.15, 48.18) * mm, "mid": v(0, 67.5) * mm, "end": v(-56.15, 48.18) * mm});
            skArc(sketch, "E79.9", {"start": v(-56.15, 48.18) * mm, "mid": v(-58.99, 44.68) * mm, "end": v(-60, 40.3) * mm});
            skLineSegment(sketch, "E79.10", {"start": v(-60, 40.3) * mm, "end": v(-60, -40.3) * mm});
            skArc(sketch, "E79.11", {"start": v(-56.15, -48.18) * mm, "mid": v(0, -67.5) * mm, "end": v(56.15, -48.18) * mm});
            skArc(sketch, "E79.12", {"start": v(-60, -40.3) * mm, "mid": v(-58.99, -44.68) * mm, "end": v(-56.15, -48.18) * mm});
            skLineSegment(sketch, "E79.13", {"start": v(60, 40.3) * mm, "end": v(60, -40.3) * mm});
            skArc(sketch, "E79.14", {"start": v(60, 40.3) * mm, "mid": v(58.99, 44.68) * mm, "end": v(56.15, 48.18) * mm});
            skArc(sketch, "E79.15", {"start": v(56.15, -48.18) * mm, "mid": v(58.99, -44.68) * mm, "end": v(60, -40.3) * mm});
            skCircle(sketch, "E79.16", {"center": v(-60, -67.5) * mm, "radius": 4 * mm});
            skCircle(sketch, "E79.17", {"center": v(-60, 67.5) * mm, "radius": 4 * mm});
            skCircle(sketch, "E79.18", {"center": v(60, 67.5) * mm, "radius": 4 * mm});
            skCircle(sketch, "E79.19", {"center": v(60, -67.5) * mm, "radius": 4 * mm});
            skPoint(sketch, "E79.20", {"position": v(60, 0) * mm});
            skLineSegment(sketch, "E80", {"start": v(-15, 108) * mm, "end": v(-15, 120) * mm});
            skArc(sketch, "E81", {"start": v(15, 120) * mm, "mid": v(0, 135) * mm, "end": v(-15, 120) * mm});
            skLineSegment(sketch, "E82", {"start": v(0, 23.75) * mm, "end": v(0, 120) * mm, "construction": true});
            skCircle(sketch, "E83", {"center": v(0, 120) * mm, "radius": 6 * mm});
            skLineSegment(sketch, "E84", {"start": v(15, 120) * mm, "end": v(15, 108) * mm});
            skLineSegment(sketch, "E85", {"start": v(15, 108) * mm, "end": v(33, 90) * mm});
            skLineSegment(sketch, "E86", {"start": v(-15, 108) * mm, "end": v(-33, 90) * mm});
            skLineSegment(sketch, "E87", {"start": v(-80, 0) * mm, "end": v(80, 0) * mm, "construction": true});
            skLineSegment(sketch, "E88.MirrorCS", {"start": v(-15, -108) * mm, "end": v(-33, -90) * mm});
            skLineSegment(sketch, "E89.MirrorCS", {"start": v(-15, -108) * mm, "end": v(-15, -120) * mm});
            skArc(sketch, "E90.MirrorCS", {"start": v(15, -120) * mm, "mid": v(0, -135) * mm, "end": v(-15, -120) * mm});
            skLineSegment(sketch, "E91.MirrorCS", {"start": v(15, -120) * mm, "end": v(15, -108) * mm});
            skLineSegment(sketch, "E92.MirrorCS", {"start": v(15, -108) * mm, "end": v(33, -90) * mm});
            skLineSegment(sketch, "E93.MirrorCS", {"start": v(0, -23.75) * mm, "end": v(0, -120) * mm, "construction": true});
            skCircle(sketch, "E94.MirrorC", {"center": v(0, -120) * mm, "radius": 6 * mm});
            skSolve(sketch);
        }
        {
            var Q0;
            {var subQ0=sQuery(id+"F16.wireOp",EDGE,"E88.MirrorCS");Q0=makeQuery(id+"F16.imprint","IMPRINT",FACE,{"disambiguationData":[TD([[makeQuery(id+"F16.imprint","IMPRINT",EDGE,{"derivedFrom":subQ0}),-1.0]])]});}
            var Q1;
            {var subQ1=sQuery(id+"F16.wireOp",EDGE,"E79.1");Q1=makeQuery(id+"F16.imprint","IMPRINT",FACE,{"disambiguationData":[TD([[makeQuery(id+"F16.imprint","IMPRINT",EDGE,{"derivedFrom":subQ1}),1.0]])]});}
            var Q2;
            {var subQ0=sQuery(id+"F16.wireOp",EDGE,"E88.MirrorCS");Q2=makeQuery(id+"F16.imprint","IMPRINT",FACE,{"disambiguationData":[TD([[makeQuery(id+"F16.imprint","IMPRINT",EDGE,{"derivedFrom":subQ0}),-1.0]])]});}
            var Q3;
            {var subQ1=sQuery(id+"F16.wireOp",EDGE,"E79.1");Q3=makeQuery(id+"F16.imprint","IMPRINT",FACE,{"disambiguationData":[TD([[makeQuery(id+"F16.imprint","IMPRINT",EDGE,{"derivedFrom":subQ1}),1.0]])]});}
            var Q4;
            Q4=makeQuery(id+"F16.imprint","IMPRINT",FACE,{"disambiguationData":[TD([[makeQuery(id+"F16.imprint","IMPRINT",EDGE,{"derivedFrom":sQuery(id+"F16.wireOp",EDGE,"E80")}),-1.0]])]});
            extrude(context, id + "F17", {"entities" : qUnion([Q0, Q1, Q2, Q3, Q4]), "operationType" : NewBodyOperationType.ADD, "depth" : 25 * mm});
        }
    });
